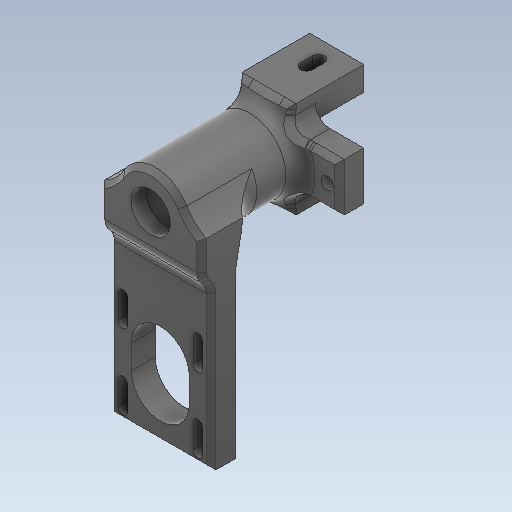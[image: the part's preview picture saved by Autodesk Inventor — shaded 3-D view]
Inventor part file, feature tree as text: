
AUTODESK INVENTOR PART (.ipt)
format: ipt  version: 2020 (Build 240168000, 168)  size: 543,744 bytes
history: native  units: mm
features: extrude x8, sketch x6, fillet x4, chamfer x4, direct_edit x2, projected_geometry x2, move_body x2, hole x1
ambient origin geometry x8: Origin, YZ Plane, XZ Plane, XY Plane, X Axis, Y Axis, Z Axis, Center Point
bodies: Solid1 (feature_tree)
feature tree (29):
  extrude  "Extrusion1"  Depth=57.0mm TaperAngle=0.0deg
  extrude  "Extrusion2"  Depth=5.2mm TaperAngle=0.0deg
  extrude  "Extrusion3"  Depth=10.0mm
  extrude  "Extrusion5"  Depth=20.0mm
  hole  "Hole1"  [1 undecoded]
  direct_edit  "Direct Edit1"
  fillet  "Fillet1"  Radius=5.0mm
  chamfer  "Chamfer1"  [1 undecoded]
  extrude  "Extrusion6"  Depth=10.0mm
  extrude  "Extrusion7"  Depth=10.0mm
  chamfer  "Chamfer2"  Distance=2.0mm Angle=45.0deg
  fillet  "Fillet2"  Radius=42.0mm
  fillet  "Fillet3"  Radius=65.0mm
  extrude  "Extrusion8"  Depth=10.0mm TaperAngle=0.0deg
  chamfer  "Chamfer3"  Distance=4.0mm
  extrude  "Extrusion9"  TaperAngle=0.0deg  [1 undecoded]
  fillet  "Fillet4"  Radius=4.0mm
  chamfer  "Chamfer4"  Distance=7.0mm
  direct_edit  "Direct Edit2"
  sketch  "Sketch1"  dims[d0=30.0mm d1=57.0mm d2=0.0mm]
  sketch  "Sketch2"  dims[d3=16.3mm d4=5.2mm d5=0.0mm]
  sketch  "Sketch3"  dims[d8=10.0mm d9=10.0mm]
  sketch  "Sketch8"  dims[d10=40.0mm d11=0.0mm d16=20.0mm]
  projected_geometry  "Projected Loop4"
  sketch  "Sketch9"  dims[d17=17.0mm d18=10.0mm d19=0.0mm d20=5.0mm]
  projected_geometry  "Projected Loop5"
  sketch  "Sketch12"  dims[d21=5.0mm d22=5.0mm d23=6.0mm d24=4.0mm d25=2.0mm d26=90.0deg d27=8.0mm d28=20.594885mm d29=0.0mm d30=0.0mm d31=-10.0mm d32=20.0mm d33=6.0mm d34=2.0mm d35=2.0mm d36=45.0deg d37=42.0mm d39=65.0mm d40=13.9mm d41=0.0mm d42=4.0mm d43=0.0mm d44=0.0mm d45=4.0mm d46=2.0mm d47=45.0deg d48=7.0mm d49=15.0mm d50=10.0mm d51=4.0mm d52=0.0mm d53=0.0mm d54=10.0mm d56=2.0mm d57=2.0mm d58=45.0deg d59=5.0mm d60=5.0mm d61=10.0mm d62=0.0mm d63=0.0mm d64=54.36068mm d65=20.0mm d66=2.0mm d67=2.0mm d68=45.0deg d69=24.0mm d70=25.0mm d71=9.5mm d72=9.5mm d73=40.5mm d74=5.5mm d75=5.5mm d76=40.5mm d77=0.0mm d78=0.0mm d79=-1.0mm d80=0.872665mm]
  move_body  "Move1"
  move_body  "Move2"
note: 3 required parameter values undecoded (feature->parameter linkage not recoverable at this tier; creation-order binding heuristic only, values carry confidence <= 0.55)
